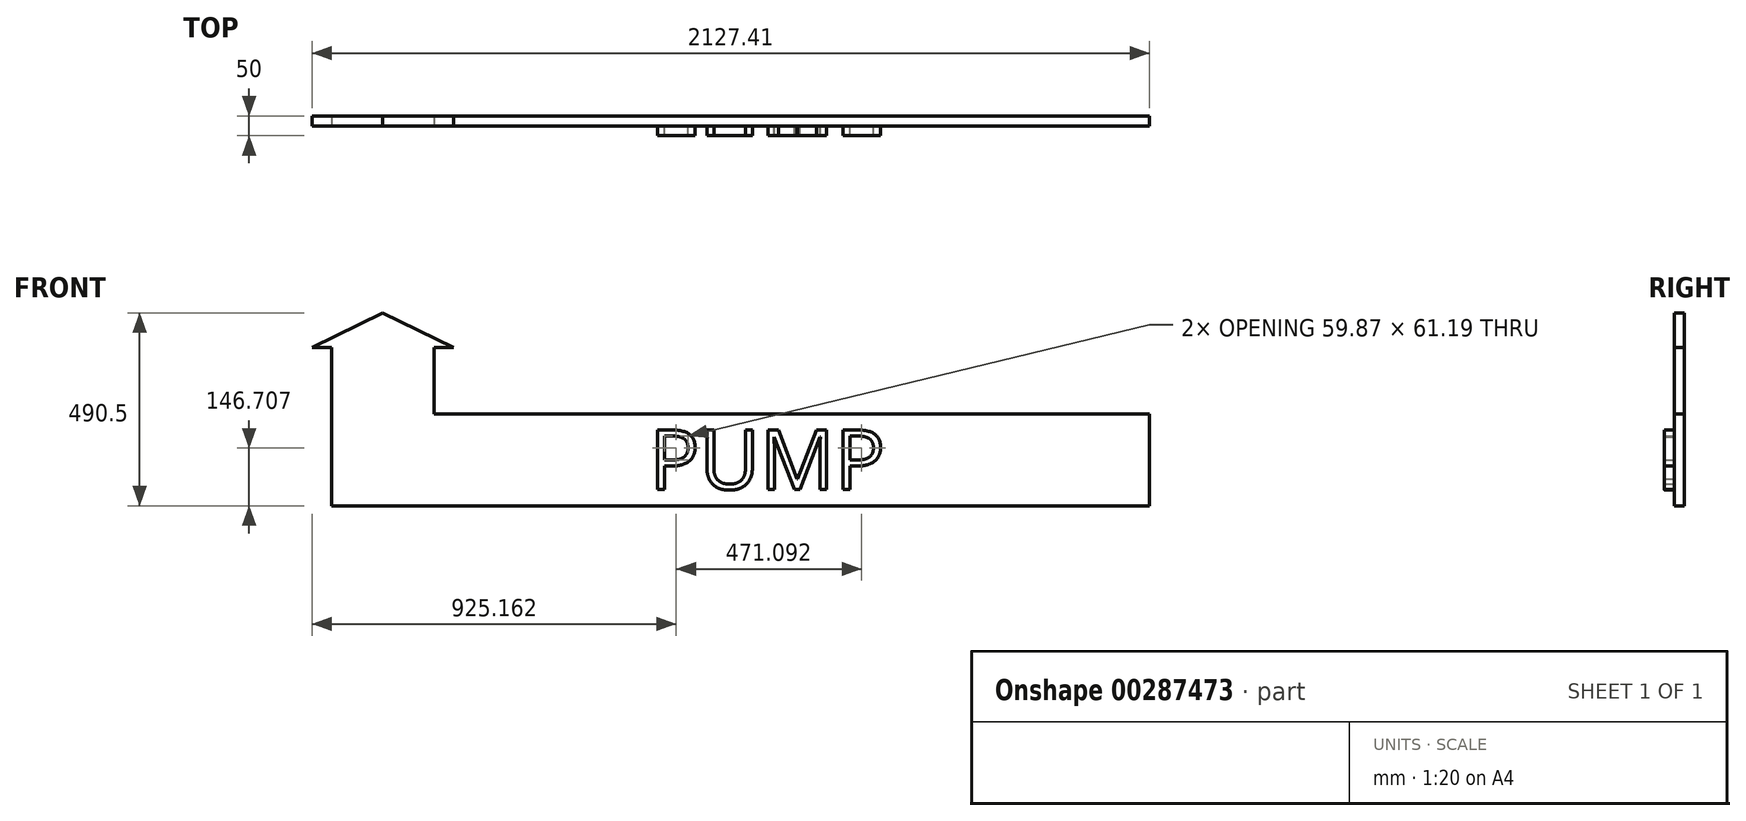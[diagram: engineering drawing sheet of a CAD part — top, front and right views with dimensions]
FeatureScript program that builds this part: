
annotation { "Feature Type Name" : "Feature", "Feature Type Description" : "" }
export const myFeature = defineFeature(function(context is Context, id is Id, definition is map)
    precondition{}
    {
        {
            var Q0;
            Q0=qCreatedBy(makeId("Front.planeOp"),FACE);
            var sketch = newSketch(context, id + "F0", { "sketchPlane" : qUnion([Q0])});
            skPoint(sketch, "E0.MirrorCS.end.orphan", {"position": v(0, 0) * mm});
            skLineSegment(sketch, "E1", {"start": v(-2046.82, 45.64) * mm, "end": v(-2046.82, 286.65) * mm});
            skPoint(sketch, "E2.MirrorCS.start.orphan", {"position": v(30.6, 279.02) * mm});
            skLineSegment(sketch, "E3", {"start": v(30.6, 279.02) * mm, "end": v(-1787.3, 279.02) * mm});
            skLineSegment(sketch, "E4", {"start": v(30.6, 279.02) * mm, "end": v(30.6, 45.64) * mm});
            skLineSegment(sketch, "E5", {"start": v(30.6, 45.64) * mm, "end": v(-2046.82, 45.64) * mm});
            skPoint(sketch, "E6", {"position": v(-2046.82, 551.1) * mm});
            skPoint(sketch, "E7.orphan", {"position": v(-1758.94, 551.1) * mm});
            skPoint(sketch, "E8.end.orphan", {"position": v(-1902.88, 551.1) * mm});
            skPoint(sketch, "E8.start.orphan", {"position": v(-2153.52, 279.02) * mm});
            skLineSegment(sketch, "E9", {"start": v(-2046.82, 286.65) * mm, "end": v(-2046.82, 448.46) * mm});
            skLineSegment(sketch, "E10", {"start": v(-2046.82, 448.46) * mm, "end": v(-2096.82, 448.46) * mm});
            skLineSegment(sketch, "E11", {"start": v(-1917.06, 536.14) * mm, "end": v(-1737.3, 448.46) * mm});
            skLineSegment(sketch, "E12", {"start": v(-1737.3, 448.46) * mm, "end": v(-1787.3, 448.46) * mm});
            skLineSegment(sketch, "E13", {"start": v(-1787.3, 448.46) * mm, "end": v(-1787.3, 279.02) * mm});
            skLineSegment(sketch, "E14", {"start": v(-1917.06, 536.14) * mm, "end": v(-2096.82, 448.46) * mm});
            skSolve(sketch);
        }
        {
            var Q0;
            Q0=qSketchRegion(id+"F0",true);
            extrude(context, id + "F1", {"entities" : qUnion([Q0]), "oppositeDirection" : true, "depth" : 25 * mm});
        }
        {
            var Q0;
            Q0=qCreatedBy(makeId("Front.planeOp"),FACE);
            var sketch = newSketch(context, id + "F2", { "sketchPlane" : qUnion([Q0])});
            skText(sketch, "E15", { "text": "PUMP", "fontName": "OpenSans-Regular.ttf"});
            const initialGuessF2  = {"E15": [-1.2398, 0.08748, 1, 0, 0.15191]};
            skSetInitialGuess(sketch, initialGuessF2);
            skSolve(sketch);
        }
        {
            var Q0;
            Q0=qSketchRegion(id+"F2",true);
            extrude(context, id + "F3", {"entities" : qUnion([Q0]), "depth" : 25 * mm});
        }
    });
